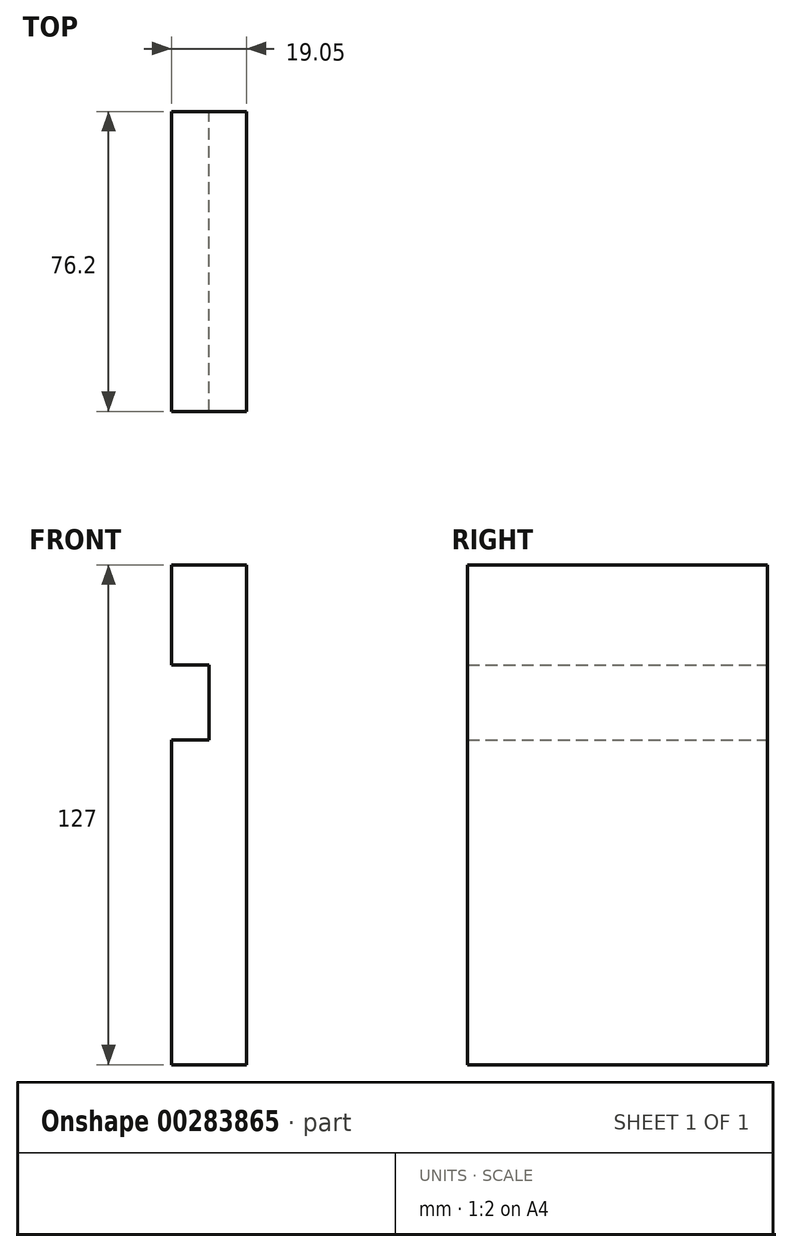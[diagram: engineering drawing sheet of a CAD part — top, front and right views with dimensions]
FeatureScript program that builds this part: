
annotation { "Feature Type Name" : "Feature", "Feature Type Description" : "" }
export const myFeature = defineFeature(function(context is Context, id is Id, definition is map)
    precondition{}
    {
        {
            var Q0;
            Q0=qCreatedBy(makeId("Front.planeOp"),FACE);
            var sketch = newSketch(context, id + "F0", { "sketchPlane" : qUnion([Q0])});
            skLineSegment(sketch, "E0", {"start": v(0, 0) * mm, "end": v(0, 127) * mm});
            skLineSegment(sketch, "E1", {"start": v(0, 127) * mm, "end": v(-19.05, 127) * mm});
            skLineSegment(sketch, "E2", {"start": v(0, 0) * mm, "end": v(-19.05, 0) * mm});
            skLineSegment(sketch, "E3", {"start": v(-19.05, 127) * mm, "end": v(-19.05, 101.6) * mm});
            skLineSegment(sketch, "E4", {"start": v(-19.05, 101.6) * mm, "end": v(-9.52, 101.6) * mm});
            skLineSegment(sketch, "E5", {"start": v(-9.52, 101.6) * mm, "end": v(-9.52, 82.55) * mm});
            skLineSegment(sketch, "E6", {"start": v(-9.52, 82.55) * mm, "end": v(-19.05, 82.55) * mm});
            skLineSegment(sketch, "E7", {"start": v(-19.05, 82.55) * mm, "end": v(-19.05, 0) * mm});
            skSolve(sketch);
        }
        {
            var Q0;
            Q0 = qSketchRegion(id + "F0", true);
            extrude(context, id + "F1", {"entities" : qUnion([Q0]), "depth" : 76.2 * mm});
        }
    });
